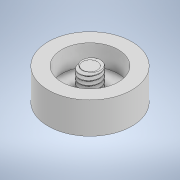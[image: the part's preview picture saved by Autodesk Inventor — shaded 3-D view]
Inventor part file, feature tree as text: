
AUTODESK INVENTOR PART (.ipt)
format: ipt  version: 2020 (Build 240168000, 168)  size: 667,648 bytes
history: native  units: in
note: dims shown in document units (in); Inventor stores cm internally (conversion verified against a paired STEP export)
features: sketch x6, extrude x3, revolve x2, thread x1, helix x1
ambient origin geometry x8: Origin, YZ Plane, XZ Plane, XY Plane, X Axis, Y Axis, Z Axis, Center Point
bodies: Solid1 (feature_tree), Solid2 (feature_tree)
feature tree (13):
  extrude  "Extrusion1"  Depth=0.375in TaperAngle=0.0deg
  extrude  "Extrusion2"  Depth=0.25in TaperAngle=0.0deg
  extrude  "Extrusion3"  Depth=0.25in TaperAngle=0.0deg
  thread  "Thread1"  [1 undecoded]
  revolve  "Revolution1"  [1 undecoded]
  revolve  "Revolution2"  [1 undecoded]
  helix  "Coil1"  [1 undecoded]
  sketch  "Sketch1"  dims[d0=1.0in d1=0.375in d2=0.0in]
  sketch  "Sketch2"  dims[d3=0.675in d4=0.25in d5=0.0in]
  sketch  "Sketch3"  dims[d6=0.25in d7=0.25in d8=0.0in d9=0.5in d10=0.0in]
  sketch  "Sketch4"  dims[d11=0.3779in d12=0.008in d13=0.008in d16=0.05in]
  sketch  "Sketch5"  dims[d18=0.3779in d20=0.0in d21=0.0in]
  sketch  "Sketch6"  dims[d22=0.05in d23=0.6in d24=0.3937in d25=0.0in d26=0.0in d27=0.0in d28=0.0in d29=0.0in]
note: 4 required parameter values undecoded (feature->parameter linkage not recoverable at this tier; creation-order binding heuristic only, values carry confidence <= 0.55)